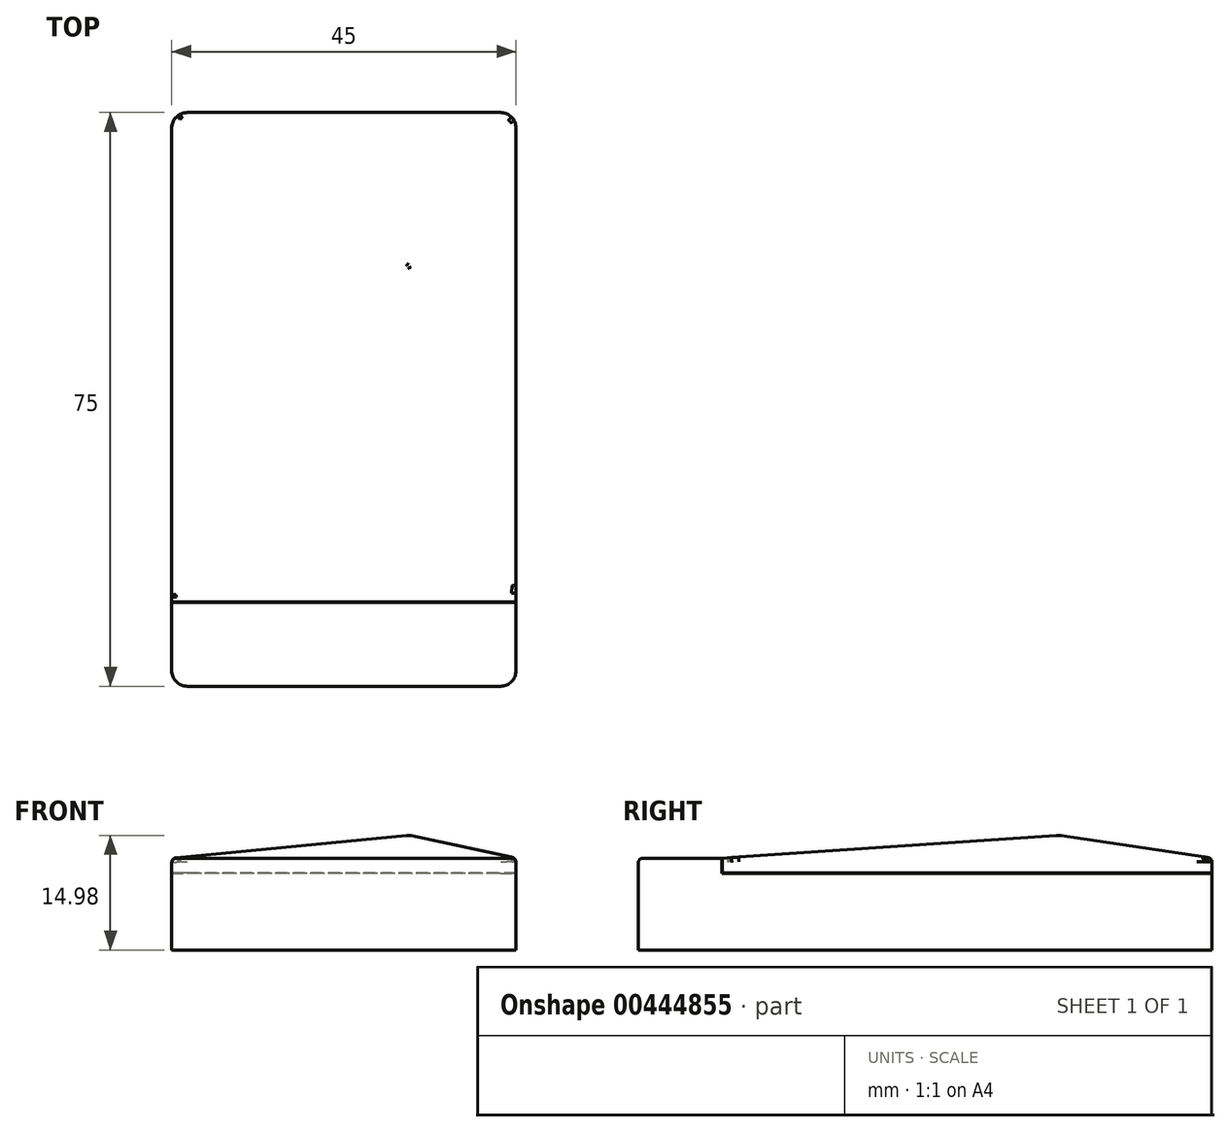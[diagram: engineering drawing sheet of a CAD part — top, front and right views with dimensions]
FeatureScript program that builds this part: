
annotation { "Feature Type Name" : "Feature", "Feature Type Description" : "" }
export const myFeature = defineFeature(function(context is Context, id is Id, definition is map)
    precondition{}
    {
        {
            var Q0;
            Q0=qCreatedBy(makeId("Top.planeOp"),FACE);
            var sketch = newSketch(context, id + "F0", { "sketchPlane" : qUnion([Q0])});
            skLineSegment(sketch, "E0.bottom", {"start": v(-22.5, 37.5) * mm, "end": v(22.5, 37.5) * mm});
            skLineSegment(sketch, "E0.top", {"start": v(-22.5, -37.5) * mm, "end": v(22.5, -37.5) * mm});
            skLineSegment(sketch, "E0.left", {"start": v(-22.5, 37.5) * mm, "end": v(-22.5, -37.5) * mm});
            skLineSegment(sketch, "E0.right", {"start": v(22.5, 37.5) * mm, "end": v(22.5, -37.5) * mm});
            skPoint(sketch, "E0.middle", {"position": v(0, 0) * mm});
            skSolve(sketch);
        }
        {
            var Q0;
            Q0=qSketchRegion(id+"F0",true);
            extrude(context, id + "F1", {"entities" : qUnion([Q0]), "depth" : 12 * mm});
        }
        {
            var Q0;
            Q0=makeQuery(id+"F1.opExtrude","CAP_FACE",FACE,{"disambiguationData":[OSD([sQuery(id+"F0.wireOp",EDGE,"E0.bottom"),sQuery(id+"F0.wireOp",EDGE,"E0.top"),sQuery(id+"F0.wireOp",EDGE,"E0.left"),sQuery(id+"F0.wireOp",EDGE,"E0.right")])],"isStart":false});
            var sketch = newSketch(context, id + "F2", { "sketchPlane" : qUnion([Q0])});
            skLineSegment(sketch, "E1.bottom", {"start": v(-22.5, 37.5) * mm, "end": v(22.5, 37.5) * mm});
            skLineSegment(sketch, "E1.top", {"start": v(-22.5, -26.5) * mm, "end": v(22.5, -26.5) * mm});
            skLineSegment(sketch, "E1.left", {"start": v(-22.5, 37.5) * mm, "end": v(-22.5, -26.5) * mm});
            skLineSegment(sketch, "E1.right", {"start": v(22.5, 37.5) * mm, "end": v(22.5, -26.5) * mm});
            skLineSegment(sketch, "E2", {"start": v(-22.5, -26.5) * mm, "end": v(8.5, 17.5) * mm});
            skLineSegment(sketch, "E3", {"start": v(8.5, 17.5) * mm, "end": v(-22.5, 37.5) * mm});
            skLineSegment(sketch, "E4", {"start": v(8.5, 17.5) * mm, "end": v(22.5, 37.5) * mm});
            skLineSegment(sketch, "E5", {"start": v(8.5, 17.5) * mm, "end": v(22.5, -26.5) * mm});
            skSolve(sketch);
        }
        {
            var Q0;
            {var subQ0=sQuery(id+"F2.wireOp",EDGE,"E1.top");Q0=makeQuery(id+"F2.imprint","IMPRINT",FACE,{"disambiguationData":[TD([[makeQuery(id+"F2.imprint","IMPRINT",EDGE,{"derivedFrom":subQ0}),-1.0]])]});}
            var sketch = newSketch(context, id + "F3", { "sketchPlane" : qUnion([Q0])});
            skLineSegment(sketch, "E6.0.0", {"start": v(-22.5, 37.5) * mm, "end": v(8.5, 17.5) * mm});
            skLineSegment(sketch, "E6.0.1", {"start": v(8.5, 17.5) * mm, "end": v(22.5, 37.5) * mm});
            skLineSegment(sketch, "E6.0.2", {"start": v(22.5, 37.5) * mm, "end": v(-22.5, 37.5) * mm});
            skSolve(sketch);
        }
        {
            var Q0;
            Q0 = qSketchRegion(id + "F3", true);
            var Q1;
            Q1=makeQuery(id+"F2.imprint","IMPRINT",FACE,{"disambiguationData":[TD([[makeQuery(id+"F2.imprint","IMPRINT",EDGE,{"derivedFrom":sQuery(id+"F2.wireOp",EDGE,"E1.bottom")}),-1.0]])]});
            extrude(context, id + "F4", {"entities" : qUnion([Q0, Q1]), "operationType" : NewBodyOperationType.ADD, "depth" : 3 * mm});
        }
        {
            var Q0;
            Q0=makeQuery(id+"F4.opExtrude","CAP_EDGE",EDGE,{"disambiguationData":[OSD([sQuery(id+"F2.wireOp",EDGE,"E1.bottom")])],"isStart":false});
            chamfer(context, id + "F5", {"entities" : qUnion([Q0]), "chamferType" : ChamferType.TWO_OFFSETS, "width1" : 3 * mm, "oppositeDirection" : false, "width2" : 20 * mm, "tangentPropagation" : true});
        }
        {
            var Q0;
            Q0=makeQuery(id+"F2.imprint","IMPRINT",FACE,{"disambiguationData":[TD([[makeQuery(id+"F2.imprint","IMPRINT",EDGE,{"derivedFrom":sQuery(id+"F2.wireOp",EDGE,"E1.right")}),-1.0]])]});
            extrude(context, id + "F6", {"entities" : qUnion([Q0]), "operationType" : NewBodyOperationType.ADD, "depth" : 3 * mm});
        }
        {
            var Q0;
            Q0=makeQuery(id+"F6.opExtrude","CAP_EDGE",EDGE,{"disambiguationData":[OSD([sQuery(id+"F2.wireOp",EDGE,"E1.right")])],"isStart":false});
            chamfer(context, id + "F7", {"entities" : qUnion([Q0]), "chamferType" : ChamferType.TWO_OFFSETS, "width1" : 3 * mm, "oppositeDirection" : false, "width2" : 14 * mm, "tangentPropagation" : true});
        }
        {
            var Q0;
            Q0=makeQuery(id+"F2.imprint","IMPRINT",FACE,{"disambiguationData":[TD([[makeQuery(id+"F2.imprint","IMPRINT",EDGE,{"derivedFrom":sQuery(id+"F2.wireOp",EDGE,"E1.top")}),1.0]])]});
            extrude(context, id + "F8", {"entities" : qUnion([Q0]), "operationType" : NewBodyOperationType.ADD, "depth" : 3 * mm});
        }
        {
            var Q0;
            Q0=makeQuery(id+"F8.opExtrude","CAP_EDGE",EDGE,{"disambiguationData":[OSD([sQuery(id+"F2.wireOp",EDGE,"E1.top")])],"isStart":false});
            chamfer(context, id + "F9", {"entities" : qUnion([Q0]), "chamferType" : ChamferType.TWO_OFFSETS, "width1" : 44 * mm, "oppositeDirection" : false, "width2" : 3 * mm, "tangentPropagation" : true});
        }
        {
            var Q0;
            Q0=makeQuery(id+"F2.imprint","IMPRINT",FACE,{"disambiguationData":[TD([[makeQuery(id+"F2.imprint","IMPRINT",EDGE,{"derivedFrom":sQuery(id+"F2.wireOp",EDGE,"E1.left")}),1.0]])]});
            extrude(context, id + "F10", {"entities" : qUnion([Q0]), "operationType" : NewBodyOperationType.ADD, "depth" : 3 * mm});
        }
        {
            var Q0;
            Q0=makeQuery(id+"F10.opExtrude","CAP_EDGE",EDGE,{"disambiguationData":[OSD([sQuery(id+"F2.wireOp",EDGE,"E1.left")])],"isStart":false});
            chamfer(context, id + "F11", {"entities" : qUnion([Q0]), "chamferType" : ChamferType.TWO_OFFSETS, "width1" : 31 * mm, "oppositeDirection" : false, "width2" : 3 * mm, "tangentPropagation" : true});
        }
        {
            var Q0;
            Q0=makeQuery(id+"F1.opExtrude","SWEPT_EDGE",EDGE,{"disambiguationData":[OSD([sQuery(id+"F0.wireOp",EDGE,"E0.bottom"),sQuery(id+"F0.wireOp",EDGE,"E0.left")])]});
            var Q1;
            Q1=makeQuery(id+"F1.opExtrude","SWEPT_EDGE",EDGE,{"disambiguationData":[OSD([sQuery(id+"F0.wireOp",EDGE,"E0.bottom"),sQuery(id+"F0.wireOp",EDGE,"E0.right")])]});
            var Q2;
            Q2=makeQuery(id+"F1.opExtrude","SWEPT_EDGE",EDGE,{"disambiguationData":[OSD([sQuery(id+"F0.wireOp",EDGE,"E0.top"),sQuery(id+"F0.wireOp",EDGE,"E0.right")])]});
            var Q3;
            Q3=makeQuery(id+"F1.opExtrude","SWEPT_EDGE",EDGE,{"disambiguationData":[OSD([sQuery(id+"F0.wireOp",EDGE,"E0.top"),sQuery(id+"F0.wireOp",EDGE,"E0.left")])]});
            fillet(context, id + "F12", {"entities" : qUnion([Q0, Q1, Q2, Q3]), "radius" : 2 * mm, "tangentPropagation" : true, "allowEdgeOverflow" : false});
        }
        {
            var Q0;
            Q0=makeQuery(id+"F10.boolean.opBoolean","MERGE",FACE,{"derivedFrom":[makeQuery(id+"F1.opExtrude","SWEPT_FACE",FACE,{"disambiguationData":[OSD([sQuery(id+"F0.wireOp",EDGE,"E0.left")])]}),makeQuery(id+"F10.opExtrude","SWEPT_FACE",FACE,{"disambiguationData":[OSD([sQuery(id+"F2.wireOp",EDGE,"E1.left")])]})]});
            var sketch = newSketch(context, id + "F13", { "sketchPlane" : qUnion([Q0])});
            skPoint(sketch, "E7.0", {"position": v(26.5, 12) * mm});
            skLineSegment(sketch, "E8", {"start": v(26.5, 12) * mm, "end": v(26.5, 10.05) * mm});
            skLineSegment(sketch, "E9", {"start": v(26.5, 10.05) * mm, "end": v(-44.97, 10.05) * mm});
            skLineSegment(sketch, "E10", {"start": v(-44.97, 10) * mm, "end": v(-44.97, 10.05) * mm});
            skLineSegment(sketch, "E11", {"start": v(-44.97, 10) * mm, "end": v(26.55, 10) * mm});
            skLineSegment(sketch, "E12", {"start": v(26.55, 10) * mm, "end": v(26.55, 12) * mm});
            skSolve(sketch);
        }
        {
            var Q0;
            {var subQ2=sQuery(id+"F13.wireOp",EDGE,"E8");Q0=makeQuery(id+"F13.imprint","IMPRINT",FACE,{"disambiguationData":[TD([[makeQuery(id+"F13.imprint","IMPRINT",EDGE,{"derivedFrom":subQ2}),1.0]])]});}
            var Q1;
            {var subQ0=sQuery(id+"F13.wireOp",EDGE,"E10");Q1=makeQuery(id+"F13.imprint","IMPRINT",FACE,{"disambiguationData":[TD([[makeQuery(id+"F13.imprint","IMPRINT",EDGE,{"derivedFrom":subQ0}),-1.0]])]});}
            extrude(context, id + "F14", {"entities" : qUnion([Q0, Q1]), "operationType" : NewBodyOperationType.REMOVE, "oppositeDirection" : true, "depth" : 50.6 * mm});
        }
        {
            var Q0;
            Q0=makeQuery(id+"F11.opChamfer","BLEND_EDGE",EDGE,{"blendedFrom":[makeQuery(id+"F10.opExtrude","CAP_EDGE",EDGE,{"disambiguationData":[OSD([sQuery(id+"F2.wireOp",EDGE,"E1.left")])],"isStart":false}),makeQuery(id+"F9.opChamfer","BLEND_FACE",FACE,{"disambiguationData":[OSD([sQuery(id+"F2.wireOp",EDGE,"E1.top")])]})],"blendedInto":[makeQuery(id+"F9.opChamfer","BLEND_FACE",FACE,{"disambiguationData":[OSD([sQuery(id+"F2.wireOp",EDGE,"E1.top")])]})]});
            var Q1;
            Q1=makeQuery(id+"F9.opChamfer","BLEND_EDGE",EDGE,{"blendedFrom":[makeQuery(id+"F8.opExtrude","CAP_EDGE",EDGE,{"disambiguationData":[OSD([sQuery(id+"F2.wireOp",EDGE,"E1.top")])],"isStart":false}),makeQuery(id+"F7.opChamfer","BLEND_FACE",FACE,{"disambiguationData":[OSD([sQuery(id+"F2.wireOp",EDGE,"E1.right")])]})],"blendedInto":[makeQuery(id+"F7.opChamfer","BLEND_FACE",FACE,{"disambiguationData":[OSD([sQuery(id+"F2.wireOp",EDGE,"E1.right")])]})]});
            var Q2;
            Q2=makeQuery(id+"F7.opChamfer","BLEND_EDGE",EDGE,{"blendedFrom":[makeQuery(id+"F6.opExtrude","CAP_EDGE",EDGE,{"disambiguationData":[OSD([sQuery(id+"F2.wireOp",EDGE,"E1.right")])],"isStart":false}),makeQuery(id+"F5.opChamfer","BLEND_FACE",FACE,{"disambiguationData":[OSD([sQuery(id+"F2.wireOp",EDGE,"E1.bottom")])]})],"blendedInto":[makeQuery(id+"F5.opChamfer","BLEND_FACE",FACE,{"disambiguationData":[OSD([sQuery(id+"F2.wireOp",EDGE,"E1.bottom")])]})]});
            var Q3;
            Q3=makeQuery(id+"F11.opChamfer","BLEND_EDGE",EDGE,{"blendedFrom":[makeQuery(id+"F10.opExtrude","CAP_EDGE",EDGE,{"disambiguationData":[OSD([sQuery(id+"F2.wireOp",EDGE,"E1.left")])],"isStart":false}),makeQuery(id+"F5.opChamfer","BLEND_FACE",FACE,{"disambiguationData":[OSD([sQuery(id+"F2.wireOp",EDGE,"E1.bottom")])]})],"blendedInto":[makeQuery(id+"F5.opChamfer","BLEND_FACE",FACE,{"disambiguationData":[OSD([sQuery(id+"F2.wireOp",EDGE,"E1.bottom")])]})]});
            fillet(context, id + "F15", {"entities" : qUnion([Q0, Q1, Q2, Q3]), "radius" : 1.9 * mm, "tangentPropagation" : true, "allowEdgeOverflow" : false});
        }
        {
            var Q0;
            {var subQ0=sQuery(id+"F2.wireOp",EDGE,"E1.bottom");Q0=makeQuery(id+"F5.opChamfer","BLEND_EDGE",EDGE,{"blendedFrom":[makeQuery(id+"F4.opExtrude","CAP_EDGE",EDGE,{"disambiguationData":[OSD([subQ0])],"isStart":false}),makeQuery(id+"F4.boolean.opBoolean","MERGE",FACE,{"derivedFrom":[makeQuery(id+"F1.opExtrude","SWEPT_FACE",FACE,{"disambiguationData":[OSD([sQuery(id+"F0.wireOp",EDGE,"E0.bottom")])]}),makeQuery(id+"F4.opExtrude","SWEPT_FACE",FACE,{"disambiguationData":[OSD([subQ0])]})]})],"blendedInto":[makeQuery(id+"F4.boolean.opBoolean","MERGE",FACE,{"derivedFrom":[makeQuery(id+"F1.opExtrude","SWEPT_FACE",FACE,{"disambiguationData":[OSD([sQuery(id+"F0.wireOp",EDGE,"E0.bottom")])]}),makeQuery(id+"F4.opExtrude","SWEPT_FACE",FACE,{"disambiguationData":[OSD([subQ0])]})]})]});}
            var Q1;
            {var subQ0=sQuery(id+"F0.wireOp",EDGE,"E0.left");var subQ1=sQuery(id+"F0.wireOp",EDGE,"E0.top");Q1=makeQuery(id+"F8.boolean.opBoolean","SPLIT",EDGE,{"disambiguationData":[TD([makeQuery(id+"F1.opExtrude","SWEPT_FACE",FACE,{"disambiguationData":[OSD([subQ1])]})])],"derivedFrom":makeQuery(id+"F1.opExtrude","CAP_EDGE",EDGE,{"disambiguationData":[OSD([subQ0])],"isStart":false})});}
            fillet(context, id + "F16", {"entities" : qUnion([Q0, Q1]), "radius" : 0.6 * mm, "tangentPropagation" : true, "allowEdgeOverflow" : false});
        }
    });
